# Revit family: Atlas_Sound_SEST_SERIES
name_source: partatom
category: Communication Devices
units: mm (PartAtom-declared; Revit-internal decimal feet)

## family parameters
Always vertical = No
Cut with Voids When Loaded = Yes
Maintain Annotation Orientation = No
Part Type = Normal
Room Calculation Point = No
Round Connector Dimension = Use Diameter
Shared = No
Work Plane-Based = Yes

## types (3) — shared parameters
Body Material = QF_Plastic - White - Smooth
Color = <By Category>
Default Elevation = 48 "
Enclosure Material = <By Category>
Family Code (default) = LOUD SPEAKER ENCLOSURES
Family Version = 2017-01
IQ Category = AUDIO VISUAL ENCLOSURES
Manufacturer = ATLAS SOUND
Manufacturer URL = https://www.atlasied.com
MasterFormat = 27 42 19
MaterFormat Title = AUDIO VISUAL ENCLOSURES
OmniClass Number = 23-37 27 15 13
OmniClass Title = Audio Visual Enclosures
Product Documentation Link = https://www.atlasied.com
Warranty = 1 Year
zero-valued in all types: Cost, Cost MSRP, Weight Product

## per-type parameters (varying)
| type | Code 1 | Code 2 | Code 3 | Depth | Description | Height | Model | Width |
| SEST-18S | Yes | No | No | 11.63 " | STRAIGHT SURFACE MOUNT ENCLOSURE IS DESIGNED FOR USE ONLY WITH ATLAS SOUND LOUDSPEAKER SYSTEM MODELS I8S AND I8SM. THE UNIT PROVIDES AN ARCHITECTURALLY PLEASING APPEARANCE WITH CRISP LINES THAT BLEND WELL WITH MOST BUILDING INTERIORS. THE ENCLOSURE IS CONSTRUCTED OF 20-GAUGE CRS AND FINISHED IN TEXTURED WHITE EPOXY. | 4 " | SEST-I8S | 11.59 " |
| SEST-18SC | No | Yes | No | 14.63 " | STRAIGHT SURFACE MOUNT ENCLOSURE IS DESIGNED FOR USE ONLY WITH ATLAS SOUND LOUDSPEAKER SYSTEM MODELS I8SC AND I8SCM. THE UNIT PROVIDES AN ARCHITECTURALLY PLEASING APPEARANCE WITH CRISP LINES THAT BLEND WELL WITH MOST BUILDING INTERIORS. THE ENCLOSURE IS CONSTRUCTED OF 20-GAUGE CRS AND FINISHED IN RECLAIMED POWDER COAT FINISH. | 4 " | SEST-I8SC | 13.13 " |
| SEST-1H | No | No | Yes | 11 " | STRAIGHT SURFACE MOUNT STAINLESS STEEL ENCLOSURE IS DESIGNED FOR USE ONLY WITH ATLAS SOUND LOUDSPEAKER SYSTEM MODEL IHVP. THE ENCLOSURE IS CONSTRUCTED OF 18-GAUGE STAINLESS STEEL AND FINISHED IN TEXTURED WHITE EPOXY. | 6 " | SEST-IH | 11 " |

## geometry (parser evidence)
native form markers: Sweep x3
no freeform markers — native parametric forms only
